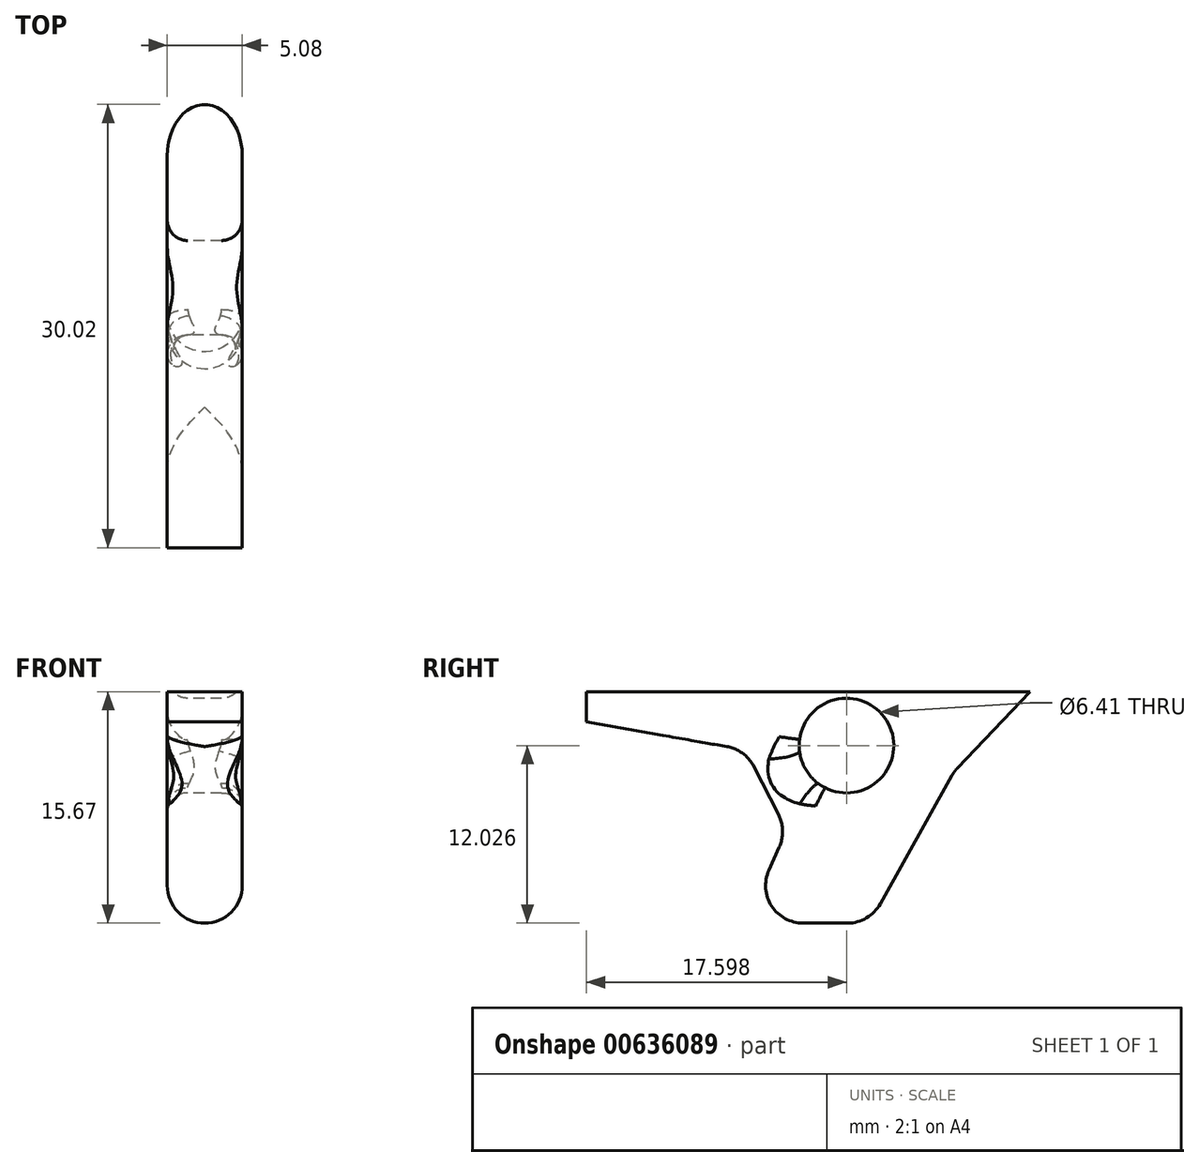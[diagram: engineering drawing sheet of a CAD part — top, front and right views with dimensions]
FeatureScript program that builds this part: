
annotation { "Feature Type Name" : "Feature", "Feature Type Description" : "" }
export const myFeature = defineFeature(function(context is Context, id is Id, definition is map)
    precondition{}
    {
        {
            var Q0;
            Q0=qCreatedBy(makeId("Right.planeOp"),FACE);
            var sketch = newSketch(context, id + "F0", { "sketchPlane" : qUnion([Q0])});
            skLineSegment(sketch, "E0", {"start": v(0, 0) * mm, "end": v(-10.75, 0) * mm});
            skLineSegment(sketch, "E1", {"start": v(0, 0) * mm, "end": v(19.27, 0) * mm});
            skLineSegment(sketch, "E2", {"start": v(19.27, 0) * mm, "end": v(14.13, -5.42) * mm});
            skLineSegment(sketch, "E3", {"start": v(14.13, -5.42) * mm, "end": v(8.4, -15.67) * mm});
            skLineSegment(sketch, "E4", {"start": v(8.4, -15.67) * mm, "end": v(0, -15.67) * mm});
            skLineSegment(sketch, "E5", {"start": v(0, -15.67) * mm, "end": v(2.8, -9.4) * mm});
            skLineSegment(sketch, "E6", {"start": v(2.8, -9.4) * mm, "end": v(0, -3.93) * mm});
            skLineSegment(sketch, "E7", {"start": v(0, -3.93) * mm, "end": v(-10.75, -2.05) * mm});
            skLineSegment(sketch, "E8", {"start": v(-10.75, -2.05) * mm, "end": v(-10.75, 0) * mm});
            skCircle(sketch, "E9", {"center": v(6.85, -3.64) * mm, "radius": 3.2 * mm});
            skLineSegment(sketch, "E10.bottom", {"start": v(-10.75, 0) * mm, "end": v(19.27, 0) * mm});
            skLineSegment(sketch, "E10.top", {"start": v(-10.75, 2.33) * mm, "end": v(19.27, 2.33) * mm});
            skLineSegment(sketch, "E10.left", {"start": v(-10.75, 0) * mm, "end": v(-10.75, 2.33) * mm});
            skLineSegment(sketch, "E10.right", {"start": v(19.27, 0) * mm, "end": v(19.27, 2.33) * mm});
            skSolve(sketch);
        }
        {
            var Q0;
            Q0=makeQuery(id+"F0.imprint","IMPRINT",FACE,{"disambiguationData":[TD([[makeQuery(id+"F0.imprint","IMPRINT",EDGE,{"derivedFrom":sQuery(id+"F0.wireOp",EDGE,"E2")}),-1.0]])]});
            var Q1;
            Q1=makeQuery(id+"F0.imprint","IMPRINT",FACE,{"disambiguationData":[TD([[makeQuery(id+"F0.imprint","IMPRINT",EDGE,{"derivedFrom":sQuery(id+"F0.wireOp",EDGE,"E10.bottom")}),1.0]])]});
            extrude(context, id + "F1", {"entities" : qUnion([Q0, Q1]), "depth" : 2.54 * mm, "offsetDistance" : 25.4 * mm});
        }
        {
            var Q0;
            Q0=makeQuery(id+"F1.opExtrude","CAP_FACE",FACE,{"disambiguationData":[OSD([sQuery(id+"F0.wireOp",EDGE,"E2"),sQuery(id+"F0.wireOp",EDGE,"E3"),sQuery(id+"F0.wireOp",EDGE,"E4"),sQuery(id+"F0.wireOp",EDGE,"E5"),sQuery(id+"F0.wireOp",EDGE,"E6"),sQuery(id+"F0.wireOp",EDGE,"E7"),sQuery(id+"F0.wireOp",EDGE,"E8"),sQuery(id+"F0.wireOp",EDGE,"E9"),sQuery(id+"F0.wireOp",EDGE,"E10.top"),sQuery(id+"F0.wireOp",EDGE,"E10.left"),sQuery(id+"F0.wireOp",EDGE,"E10.right")])],"isStart":true});
            extrude(context, id + "F2", {"entities" : qUnion([Q0]), "operationType" : NewBodyOperationType.ADD, "depth" : 2.54 * mm, "offsetDistance" : 25.4 * mm});
        }
        {
            var Q0;
            Q0=makeQuery(id+"F2.opExtrude","CAP_EDGE",EDGE,{"disambiguationData":[OSD([sQuery(id+"F0.wireOp",EDGE,"E2")])],"isStart":false});
            var Q1;
            Q1=makeQuery(id+"F1.opExtrude","CAP_EDGE",EDGE,{"disambiguationData":[OSD([sQuery(id+"F0.wireOp",EDGE,"E2")])],"isStart":false});
            var Q2;
            Q2=makeQuery(id+"F1.opExtrude","CAP_EDGE",EDGE,{"disambiguationData":[OSD([sQuery(id+"F0.wireOp",EDGE,"E3")])],"isStart":false});
            var Q3;
            Q3=makeQuery(id+"F2.opExtrude","CAP_EDGE",EDGE,{"disambiguationData":[OSD([sQuery(id+"F0.wireOp",EDGE,"E3")])],"isStart":false});
            var Q4;
            {var subQ0=sQuery(id+"F0.wireOp",EDGE,"E4");var subQ1=sQuery(id+"F0.wireOp",EDGE,"E3");Q4=makeQuery(id+"F2.boolean.opBoolean","MERGE",EDGE,{"derivedFrom":[makeQuery(id+"F1.opExtrude","SWEPT_EDGE",EDGE,{"disambiguationData":[OSD([subQ1,subQ0])]}),makeQuery(id+"F2.opExtrude","SWEPT_EDGE",EDGE,{"disambiguationData":[OSD([subQ1,subQ0])]})]});}
            var Q5;
            Q5=makeQuery(id+"F1.opExtrude","CAP_EDGE",EDGE,{"disambiguationData":[OSD([sQuery(id+"F0.wireOp",EDGE,"E4")])],"isStart":false});
            var Q6;
            Q6=makeQuery(id+"F2.opExtrude","CAP_EDGE",EDGE,{"disambiguationData":[OSD([sQuery(id+"F0.wireOp",EDGE,"E4")])],"isStart":false});
            var Q7;
            {var subQ0=sQuery(id+"F0.wireOp",EDGE,"E5");var subQ1=sQuery(id+"F0.wireOp",EDGE,"E4");Q7=makeQuery(id+"F2.boolean.opBoolean","MERGE",EDGE,{"derivedFrom":[makeQuery(id+"F1.opExtrude","SWEPT_EDGE",EDGE,{"disambiguationData":[OSD([subQ1,subQ0])]}),makeQuery(id+"F2.opExtrude","SWEPT_EDGE",EDGE,{"disambiguationData":[OSD([subQ1,subQ0])]})]});}
            var Q8;
            Q8=makeQuery(id+"F1.opExtrude","CAP_EDGE",EDGE,{"disambiguationData":[OSD([sQuery(id+"F0.wireOp",EDGE,"E5")])],"isStart":false});
            var Q9;
            Q9=makeQuery(id+"F2.opExtrude","CAP_EDGE",EDGE,{"disambiguationData":[OSD([sQuery(id+"F0.wireOp",EDGE,"E5")])],"isStart":false});
            var Q10;
            Q10=makeQuery(id+"F1.opExtrude","CAP_EDGE",EDGE,{"disambiguationData":[OSD([sQuery(id+"F0.wireOp",EDGE,"E6")])],"isStart":false});
            var Q11;
            Q11=makeQuery(id+"F2.opExtrude","CAP_EDGE",EDGE,{"disambiguationData":[OSD([sQuery(id+"F0.wireOp",EDGE,"E6")])],"isStart":false});
            var Q12;
            {var subQ0=sQuery(id+"F0.wireOp",EDGE,"E7");var subQ1=sQuery(id+"F0.wireOp",EDGE,"E6");Q12=makeQuery(id+"F2.boolean.opBoolean","MERGE",EDGE,{"derivedFrom":[makeQuery(id+"F1.opExtrude","SWEPT_EDGE",EDGE,{"disambiguationData":[OSD([subQ1,subQ0])]}),makeQuery(id+"F2.opExtrude","SWEPT_EDGE",EDGE,{"disambiguationData":[OSD([subQ1,subQ0])]})]});}
            var Q13;
            {var subQ0=sQuery(id+"F0.wireOp",EDGE,"E3");var subQ1=sQuery(id+"F0.wireOp",EDGE,"E2");Q13=makeQuery(id+"F2.boolean.opBoolean","MERGE",EDGE,{"derivedFrom":[makeQuery(id+"F1.opExtrude","SWEPT_EDGE",EDGE,{"disambiguationData":[OSD([subQ1,subQ0])]}),makeQuery(id+"F2.opExtrude","SWEPT_EDGE",EDGE,{"disambiguationData":[OSD([subQ1,subQ0])]})]});}
            var Q14;
            {var subQ0=sQuery(id+"F0.wireOp",EDGE,"E6");var subQ1=sQuery(id+"F0.wireOp",EDGE,"E5");Q14=makeQuery(id+"F2.boolean.opBoolean","MERGE",EDGE,{"derivedFrom":[makeQuery(id+"F1.opExtrude","SWEPT_EDGE",EDGE,{"disambiguationData":[OSD([subQ1,subQ0])]}),makeQuery(id+"F2.opExtrude","SWEPT_EDGE",EDGE,{"disambiguationData":[OSD([subQ1,subQ0])]})]});}
            fillet(context, id + "F3", {"entities" : qUnion([Q0, Q1, Q2, Q3, Q4, Q5, Q6, Q7, Q8, Q9, Q10, Q11, Q12, Q13, Q14]), "radius" : 2.54 * mm, "tangentPropagation" : true, "allowEdgeOverflow" : false});
        }
        {
            var Q0;
            Q0=makeQuery(id+"F1.opExtrude","CAP_EDGE",EDGE,{"disambiguationData":[OSD([sQuery(id+"F0.wireOp",EDGE,"E9")])],"isStart":false});
            var Q1;
            Q1=makeQuery(id+"F2.opExtrude","CAP_EDGE",EDGE,{"disambiguationData":[OSD([sQuery(id+"F0.wireOp",EDGE,"E9")])],"isStart":false});
            fillet(context, id + "F4", {"entities" : qUnion([Q0, Q1]), "radius" : 1.4 * mm, "tangentPropagation" : true, "allowEdgeOverflow" : false});
        }
    });
